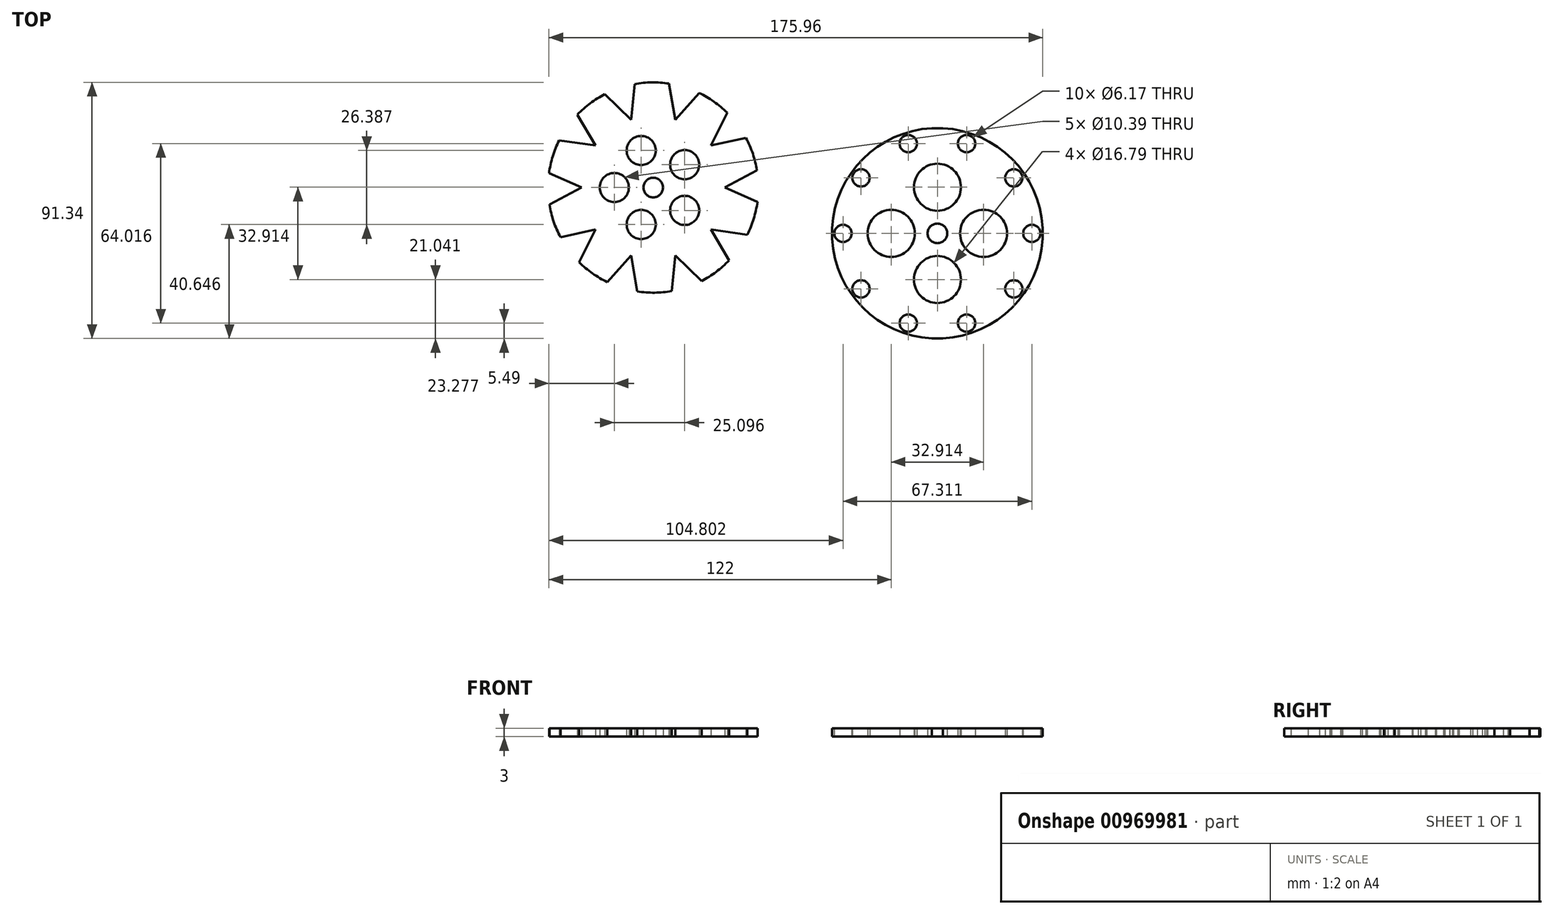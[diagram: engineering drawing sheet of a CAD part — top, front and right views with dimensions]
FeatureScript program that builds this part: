
annotation { "Feature Type Name" : "Feature", "Feature Type Description" : "" }
export const myFeature = defineFeature(function(context is Context, id is Id, definition is map)
    precondition{}
    {
        {
            var Q0;
            Q0=qCreatedBy(makeId("Top.planeOp"),FACE);
            var sketch = newSketch(context, id + "F0", { "sketchPlane" : qUnion([Q0])});
            skLineSegment(sketch, "E0.bottom", {"start": v(37.5, -37.5) * mm, "end": v(-37.5, -37.5) * mm});
            skLineSegment(sketch, "E0.top", {"start": v(37.5, 37.5) * mm, "end": v(-37.5, 37.5) * mm});
            skLineSegment(sketch, "E0.left", {"start": v(37.5, -37.5) * mm, "end": v(37.5, 37.5) * mm});
            skLineSegment(sketch, "E0.right", {"start": v(-37.5, -37.5) * mm, "end": v(-37.5, 37.5) * mm});
            skPoint(sketch, "E0.middle", {"position": v(0, 0) * mm});
            skCircle(sketch, "E1", {"center": v(0, 0) * mm, "radius": 3.5 * mm});
            skCircle(sketch, "E2", {"center": v(0, 0) * mm, "radius": 37.5 * mm});
            skLineSegment(sketch, "E3", {"start": v(-37, -6.07) * mm, "end": v(-25.48, 0) * mm});
            skLineSegment(sketch, "E4", {"start": v(-25.48, 0) * mm, "end": v(-37.15, 5.13) * mm});
            skLineSegment(sketch, "E5.1.0", {"start": v(-26.37, -26.67) * mm, "end": v(-20.61, -14.98) * mm});
            skLineSegment(sketch, "E5.1.1", {"start": v(-20.61, -14.98) * mm, "end": v(-33.07, -17.69) * mm});
            skLineSegment(sketch, "E5.2.0", {"start": v(-5.66, -37.07) * mm, "end": v(-7.87, -24.23) * mm});
            skLineSegment(sketch, "E5.2.1", {"start": v(-7.87, -24.23) * mm, "end": v(-16.36, -33.74) * mm});
            skLineSegment(sketch, "E5.3.0", {"start": v(17.21, -33.32) * mm, "end": v(7.87, -24.23) * mm});
            skLineSegment(sketch, "E5.3.1", {"start": v(7.87, -24.23) * mm, "end": v(6.6, -36.91) * mm});
            skLineSegment(sketch, "E5.4.0", {"start": v(33.5, -16.84) * mm, "end": v(20.61, -14.98) * mm});
            skLineSegment(sketch, "E5.4.1", {"start": v(20.61, -14.98) * mm, "end": v(27.04, -25.98) * mm});
            skLineSegment(sketch, "E5.5.0", {"start": v(37, 6.07) * mm, "end": v(25.48, 0) * mm});
            skLineSegment(sketch, "E5.5.1", {"start": v(25.48, 0) * mm, "end": v(37.15, -5.13) * mm});
            skLineSegment(sketch, "E5.6.0", {"start": v(26.37, 26.67) * mm, "end": v(20.61, 14.98) * mm});
            skLineSegment(sketch, "E5.6.1", {"start": v(20.61, 14.98) * mm, "end": v(33.07, 17.69) * mm});
            skLineSegment(sketch, "E5.7.0", {"start": v(5.66, 37.07) * mm, "end": v(7.87, 24.23) * mm});
            skLineSegment(sketch, "E5.7.1", {"start": v(7.87, 24.23) * mm, "end": v(16.36, 33.74) * mm});
            skLineSegment(sketch, "E5.8.0", {"start": v(-17.21, 33.32) * mm, "end": v(-7.87, 24.23) * mm});
            skLineSegment(sketch, "E5.8.1", {"start": v(-7.87, 24.23) * mm, "end": v(-6.6, 36.91) * mm});
            skLineSegment(sketch, "E5.9.0", {"start": v(-33.5, 16.84) * mm, "end": v(-20.61, 14.98) * mm});
            skLineSegment(sketch, "E5.9.1", {"start": v(-20.61, 14.98) * mm, "end": v(-27.04, 25.98) * mm});
            skCircle(sketch, "E6", {"center": v(-13.87, 0) * mm, "radius": 5.2 * mm});
            skCircle(sketch, "E7.1.0", {"center": v(-4.29, -13.2) * mm, "radius": 5.2 * mm});
            skCircle(sketch, "E7.2.0", {"center": v(11.22, -8.15) * mm, "radius": 5.2 * mm});
            skCircle(sketch, "E7.3.0", {"center": v(11.22, 8.15) * mm, "radius": 5.2 * mm});
            skCircle(sketch, "E7.4.0", {"center": v(-4.29, 13.2) * mm, "radius": 5.2 * mm});
            skSolve(sketch);
        }
        {
            var Q0;
            Q0=makeQuery(id+"F0.imprint","IMPRINT",FACE,{"disambiguationData":[TD([[makeQuery(id+"F0.imprint","IMPRINT",EDGE,{"derivedFrom":sQuery(id+"F0.wireOp",EDGE,"E1")}),-1.0]])]});
            extrude(context, id + "F1", {"entities" : qUnion([Q0]), "depth" : 3 * mm, "offsetDistance" : 25 * mm});
        }
        {
            var Q0;
            Q0=qCreatedBy(makeId("Top.planeOp"),FACE);
            var sketch = newSketch(context, id + "F2", { "sketchPlane" : qUnion([Q0])});
            skLineSegment(sketch, "E8.bottom", {"start": v(138.8, -53.84) * mm, "end": v(63.8, -53.84) * mm});
            skLineSegment(sketch, "E8.top", {"start": v(138.8, 21.16) * mm, "end": v(63.8, 21.16) * mm});
            skLineSegment(sketch, "E8.left", {"start": v(138.8, -53.84) * mm, "end": v(138.8, 21.16) * mm});
            skLineSegment(sketch, "E8.right", {"start": v(63.8, -53.84) * mm, "end": v(63.8, 21.16) * mm});
            skCircle(sketch, "E9", {"center": v(101.3, -16.34) * mm, "radius": 3.5 * mm});
            skPoint(sketch, "E9.centerSnap0", {"position": v(138.8, -16.34) * mm});
            skPoint(sketch, "E9.centerSnap1", {"position": v(101.3, -53.84) * mm});
            skCircle(sketch, "E10", {"center": v(101.3, -16.34) * mm, "radius": 37.55 * mm});
            skCircle(sketch, "E11", {"center": v(67.65, -16.34) * mm, "radius": 3.09 * mm});
            skCircle(sketch, "E12.1.0", {"center": v(74.08, -36.12) * mm, "radius": 3.09 * mm});
            skCircle(sketch, "E12.2.0", {"center": v(90.9, -48.35) * mm, "radius": 3.09 * mm});
            skCircle(sketch, "E12.3.0", {"center": v(111.7, -48.35) * mm, "radius": 3.09 * mm});
            skCircle(sketch, "E12.4.0", {"center": v(128.53, -36.12) * mm, "radius": 3.09 * mm});
            skCircle(sketch, "E12.5.0", {"center": v(134.96, -16.34) * mm, "radius": 3.09 * mm});
            skCircle(sketch, "E12.6.0", {"center": v(128.53, 3.44) * mm, "radius": 3.09 * mm});
            skCircle(sketch, "E12.7.0", {"center": v(111.7, 15.67) * mm, "radius": 3.09 * mm});
            skCircle(sketch, "E12.8.0", {"center": v(90.9, 15.67) * mm, "radius": 3.09 * mm});
            skCircle(sketch, "E12.9.0", {"center": v(74.08, 3.44) * mm, "radius": 3.09 * mm});
            skCircle(sketch, "E13", {"center": v(84.85, -16.34) * mm, "radius": 8.4 * mm});
            skCircle(sketch, "E14.1.0", {"center": v(101.3, -32.8) * mm, "radius": 8.4 * mm});
            skCircle(sketch, "E14.2.0", {"center": v(117.76, -16.34) * mm, "radius": 8.4 * mm});
            skCircle(sketch, "E14.3.0", {"center": v(101.3, 0.11) * mm, "radius": 8.4 * mm});
            skSolve(sketch);
        }
        {
            var Q0;
            Q0=makeQuery(id+"F2.imprint","IMPRINT",FACE,{"disambiguationData":[TD([[makeQuery(id+"F2.imprint","IMPRINT",EDGE,{"derivedFrom":sQuery(id+"F2.wireOp",EDGE,"E9")}),-1.0]])]});
            extrude(context, id + "F3", {"entities" : qUnion([Q0]), "depth" : 3 * mm, "offsetDistance" : 25 * mm});
        }
    });
